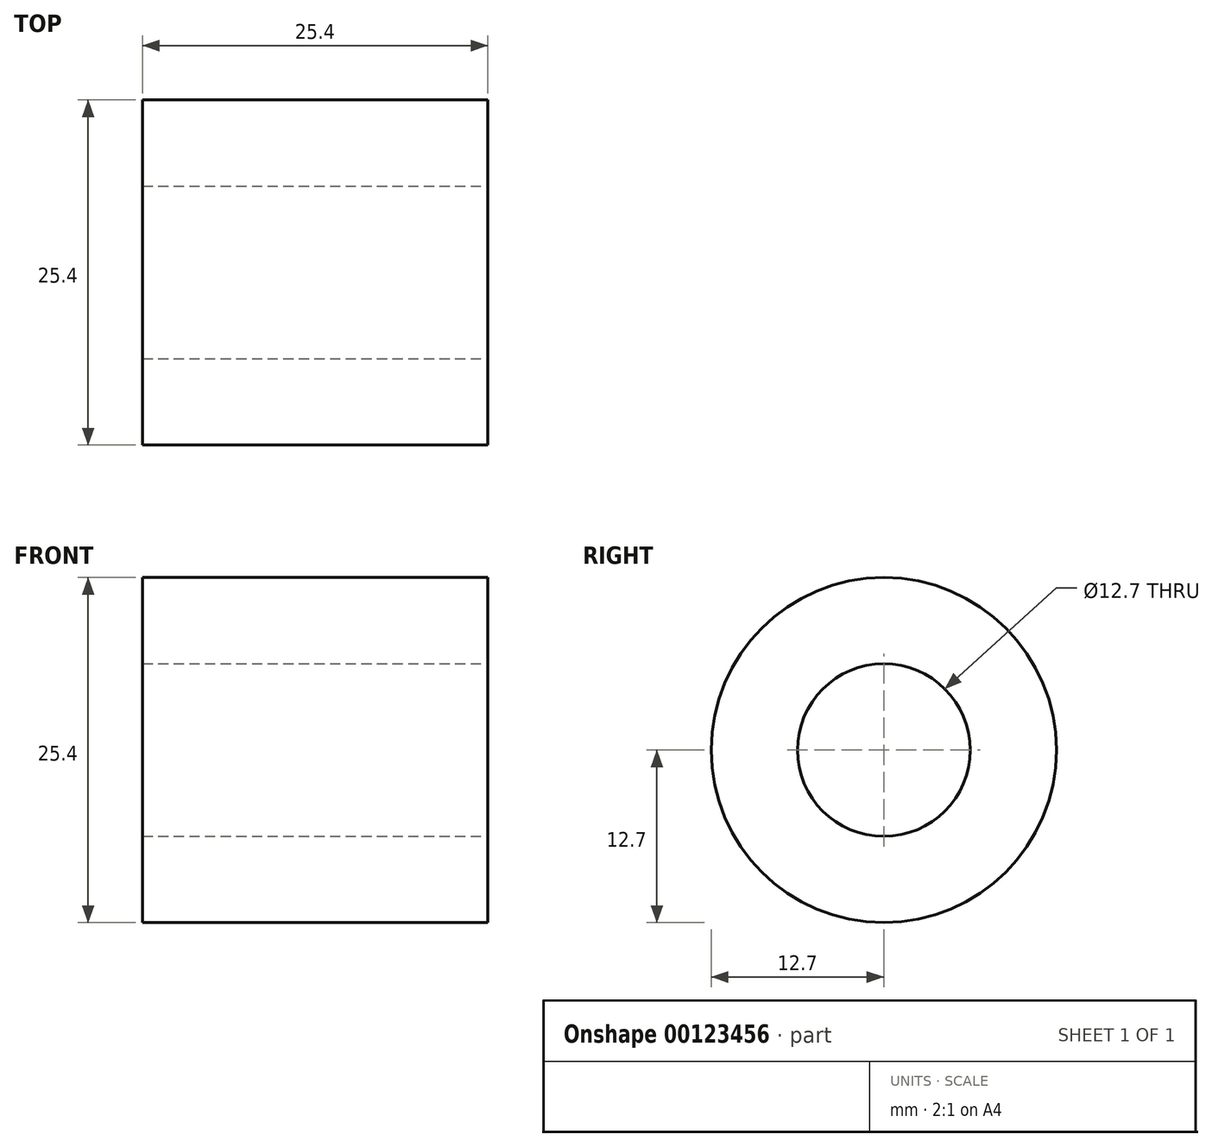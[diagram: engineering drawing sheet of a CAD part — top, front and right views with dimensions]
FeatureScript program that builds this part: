
annotation { "Feature Type Name" : "Feature", "Feature Type Description" : "" }
export const myFeature = defineFeature(function(context is Context, id is Id, definition is map)
    precondition{}
    {
        {
            var Q0;
            Q0=qCreatedBy(makeId("Top.planeOp"),FACE);
            var sketch = newSketch(context, id + "F0", { "sketchPlane" : qUnion([Q0])});
            skLineSegment(sketch, "E0", {"start": v(-25.4, 0) * mm, "end": v(-25.4, 12.7) * mm});
            skLineSegment(sketch, "E1", {"start": v(-25.4, 12.7) * mm, "end": v(0, 12.7) * mm});
            skLineSegment(sketch, "E2", {"start": v(0, 12.7) * mm, "end": v(0, 0) * mm});
            skLineSegment(sketch, "E3", {"start": v(-25.4, 0) * mm, "end": v(0, 0) * mm});
            skSolve(sketch);
        }
        {
            var Q0;
            Q0=qSketchRegion(id+"F0",true);
            var Q1;
            Q1=sQuery(id+"F0.wireOp",EDGE,"E3");
            revolve(context, id + "F1", {"entities" : qUnion([Q0]), "axis" : qUnion([Q1]), "revolveType" : RevolveType.FULL});
        }
        {
            var Q0;
            Q0=makeQuery(id+"F1.opRevolve","SWEPT_FACE",FACE,{"disambiguationData":[OSD([sQuery(id+"F0.wireOp",EDGE,"E2")])]});
            var sketch = newSketch(context, id + "F2", { "sketchPlane" : qUnion([Q0])});
            skCircle(sketch, "E4", {"center": v(0, 0) * mm, "radius": 6.35 * mm});
            skSolve(sketch);
        }
        {
            var Q0;
            Q0 = qSketchRegion(id + "F2", true);
            extrude(context, id + "F3", {"entities" : qUnion([Q0]), "operationType" : NewBodyOperationType.REMOVE, "endBound" : BoundingType.THROUGH_ALL, "oppositeDirection" : true, "depth" : 25.4 * mm});
        }
    });
